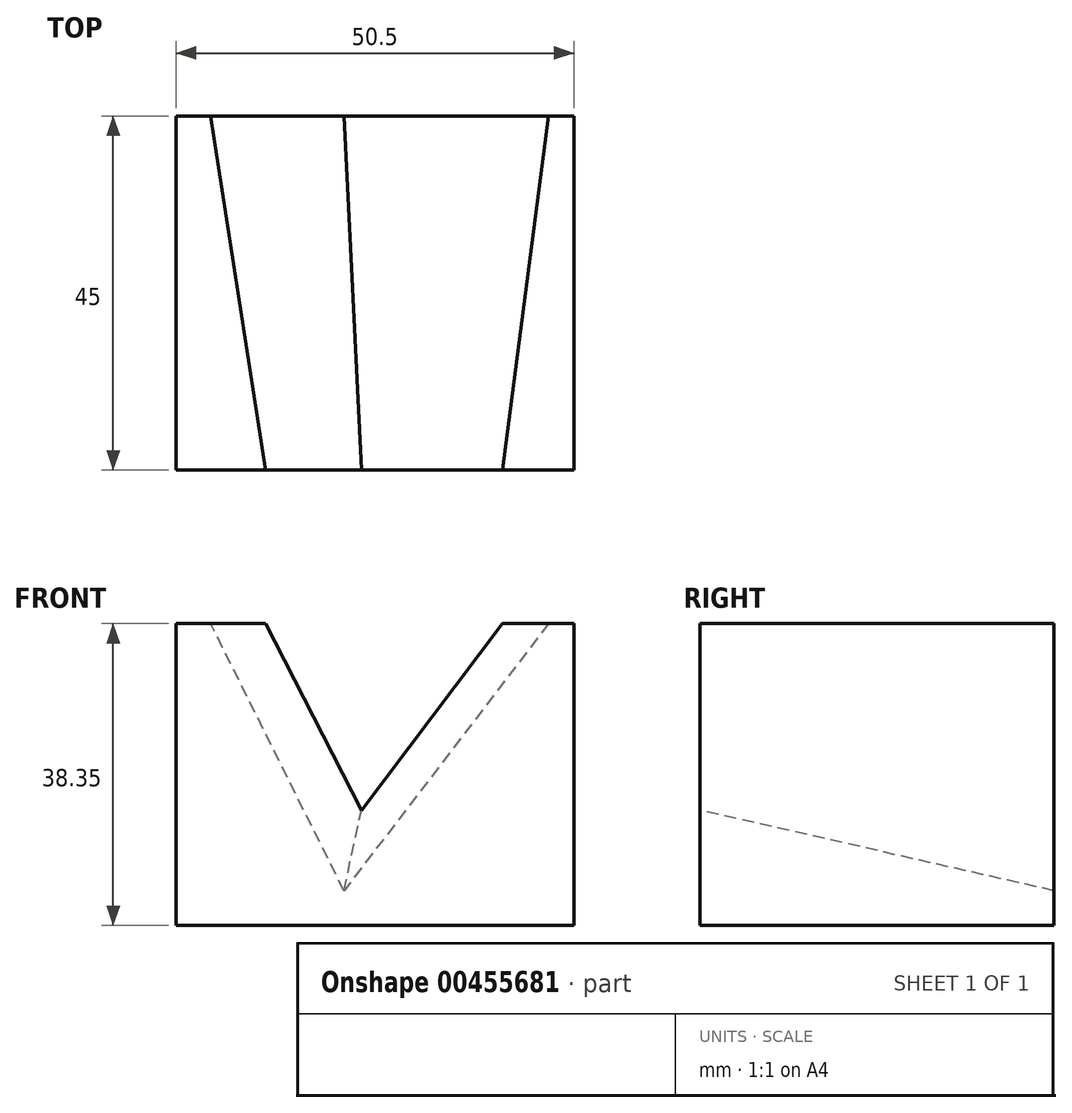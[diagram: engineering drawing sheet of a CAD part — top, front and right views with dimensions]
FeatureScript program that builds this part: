
annotation { "Feature Type Name" : "Feature", "Feature Type Description" : "" }
export const myFeature = defineFeature(function(context is Context, id is Id, definition is map)
    precondition{}
    {
        {
            var Q0;
            Q0=qCreatedBy(makeId("Top.planeOp"),FACE);
            var sketch = newSketch(context, id + "F0", { "sketchPlane" : qUnion([Q0])});
            skLineSegment(sketch, "E0.bottom", {"start": v(0, 0) * mm, "end": v(50.5, 0) * mm});
            skLineSegment(sketch, "E0.top", {"start": v(0, -45) * mm, "end": v(50.5, -45) * mm});
            skLineSegment(sketch, "E0.left", {"start": v(0, 0) * mm, "end": v(0, -45) * mm});
            skLineSegment(sketch, "E0.right", {"start": v(50.5, 0) * mm, "end": v(50.5, -45) * mm});
            skSolve(sketch);
        }
        {
            var Q0;
            Q0=makeQuery(id+"F0.imprint","IMPRINT",FACE,{"disambiguationData":[TD([[makeQuery(id+"F0.imprint","IMPRINT",EDGE,{"derivedFrom":sQuery(id+"F0.wireOp",EDGE,"E0.bottom")}),-1.0]])]});
            extrude(context, id + "F1", {"entities" : qUnion([Q0]), "depth" : 38.35 * mm});
        }
        {
            var Q0;
            Q0=makeQuery(id+"F1.opExtrude","SWEPT_FACE",FACE,{"disambiguationData":[OSD([sQuery(id+"F0.wireOp",EDGE,"E0.top")])]});
            var sketch = newSketch(context, id + "F2", { "sketchPlane" : qUnion([Q0])});
            skLineSegment(sketch, "E1", {"start": v(11.34, 38.35) * mm, "end": v(23.5, 14.64) * mm});
            skLineSegment(sketch, "E2", {"start": v(23.5, 14.64) * mm, "end": v(41.45, 38.35) * mm});
            skSolve(sketch);
        }
        {
            var Q0;
            Q0=makeQuery(id+"F1.opExtrude","SWEPT_FACE",FACE,{"disambiguationData":[OSD([sQuery(id+"F0.wireOp",EDGE,"E0.bottom")])]});
            var sketch = newSketch(context, id + "F3", { "sketchPlane" : qUnion([Q0])});
            skLineSegment(sketch, "E3", {"start": v(-47.3, 38.35) * mm, "end": v(-21.31, 4.42) * mm});
            skLineSegment(sketch, "E4", {"start": v(-21.31, 4.42) * mm, "end": v(-4.37, 38.35) * mm});
            skSolve(sketch);
        }
        {
            var Q1;
            {var subQ0=sQuery(id+"F3.wireOp",EDGE,"E3");Q1=makeQuery(id+"F3.imprint","IMPRINT",FACE,{"disambiguationData":[TD([[makeQuery(id+"F3.imprint","IMPRINT",EDGE,{"derivedFrom":subQ0}),1.0]])]});}
            var Q2;
            {var subQ0=sQuery(id+"F2.wireOp",EDGE,"E1");Q2=makeQuery(id+"F2.imprint","IMPRINT",FACE,{"disambiguationData":[TD([[makeQuery(id+"F2.imprint","IMPRINT",EDGE,{"derivedFrom":subQ0}),1.0]])]});}
            loft(context, id + "F4", {"operationType" : NewBodyOperationType.REMOVE, "sheetProfilesArray" : [{ "sheetProfileEntities" : qUnion([Q1]) }, { "sheetProfileEntities" : qUnion([Q2]) }]});
        }
    });
